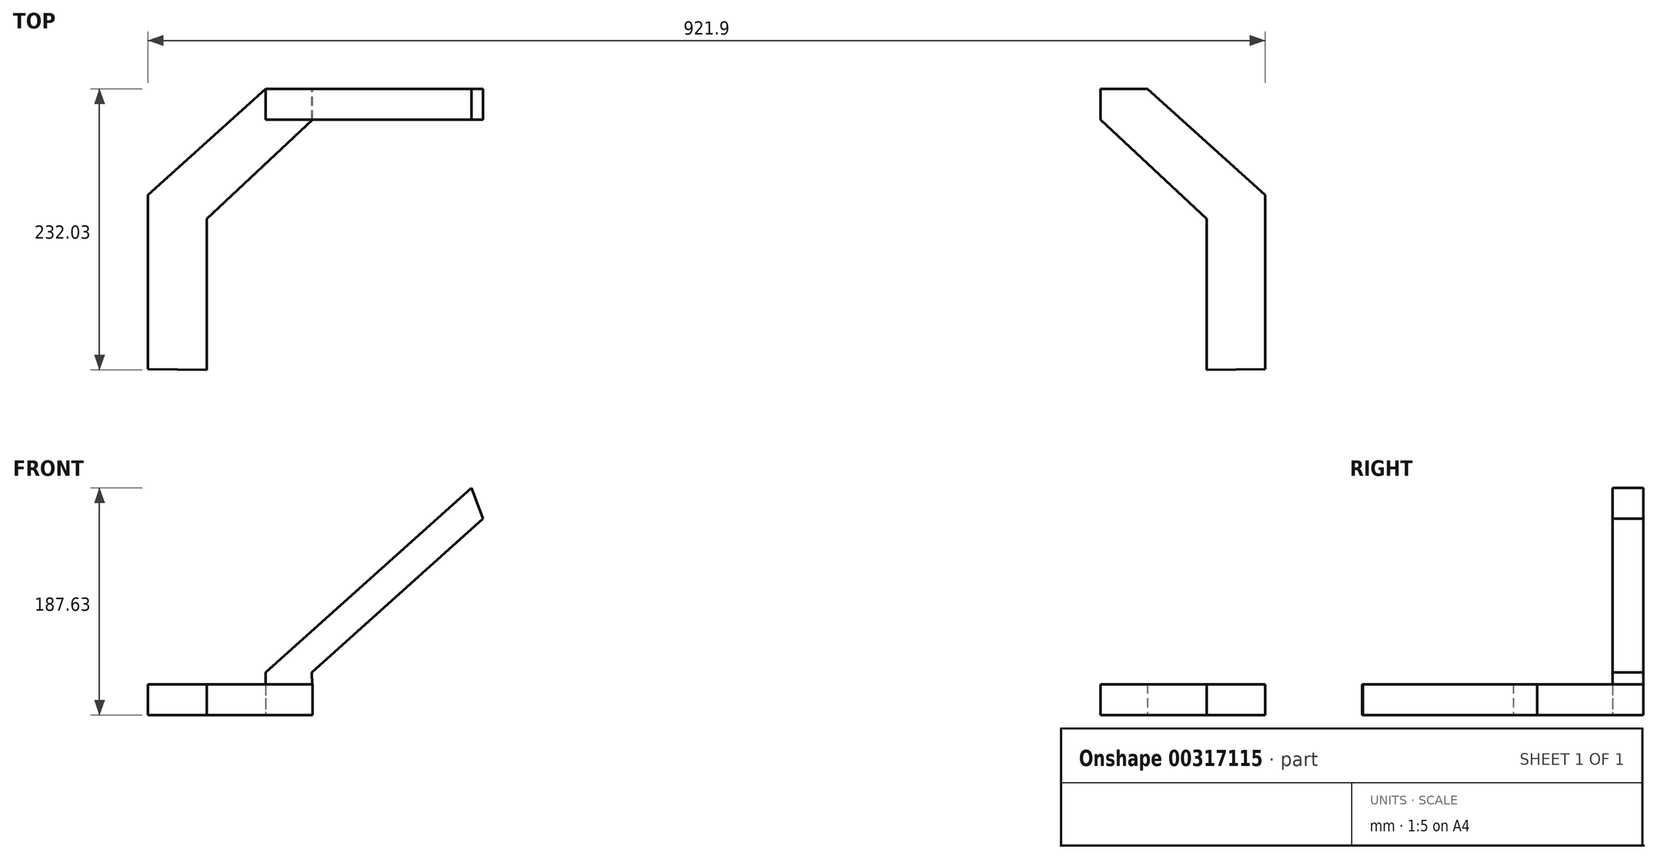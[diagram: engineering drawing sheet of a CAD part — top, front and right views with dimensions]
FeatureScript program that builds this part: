
annotation { "Feature Type Name" : "Feature", "Feature Type Description" : "" }
export const myFeature = defineFeature(function(context is Context, id is Id, definition is map)
    precondition{}
    {
        {
            var Q0;
            Q0=qCreatedBy(makeId("Front.planeOp"),FACE);
            var sketch = newSketch(context, id + "F0", { "sketchPlane" : qUnion([Q0])});
            skLineSegment(sketch, "E0.bottom", {"start": v(0, 127) * mm, "end": v(-184.37, 127) * mm});
            skLineSegment(sketch, "E0.top", {"start": v(0, 152.4) * mm, "end": v(-194.1, 152.4) * mm});
            skLineSegment(sketch, "E0.right", {"start": v(-184.37, 127) * mm, "end": v(-194.1, 152.4) * mm});
            skPoint(sketch, "E0.middle", {"position": v(0, 112.8) * mm});
            skLineSegment(sketch, "E1", {"start": v(-194.1, 152.4) * mm, "end": v(-363.8, 0) * mm});
            skLineSegment(sketch, "E2", {"start": v(-325.78, 0) * mm, "end": v(-184.37, 127) * mm});
            skLineSegment(sketch, "E3", {"start": v(0, 152.4) * mm, "end": v(0, 127) * mm});
            skLineSegment(sketch, "E4", {"start": v(-363.8, 0) * mm, "end": v(-363.8, -35.23) * mm});
            skLineSegment(sketch, "E5", {"start": v(-363.8, -35.23) * mm, "end": v(-325, -35.23) * mm});
            skLineSegment(sketch, "E6", {"start": v(-325, -35.23) * mm, "end": v(-325.78, 0) * mm});
            skLineSegment(sketch, "E7.MirrorCS", {"start": v(0, 152.4) * mm, "end": v(194.1, 152.4) * mm});
            skLineSegment(sketch, "E8.MirrorCS", {"start": v(194.1, 152.4) * mm, "end": v(363.8, 0) * mm});
            skLineSegment(sketch, "E9.MirrorCS", {"start": v(363.8, 0) * mm, "end": v(363.8, -35.23) * mm});
            skLineSegment(sketch, "E10.MirrorCS", {"start": v(363.8, -35.23) * mm, "end": v(325, -35.23) * mm});
            skLineSegment(sketch, "E11.MirrorCS", {"start": v(325, -35.23) * mm, "end": v(325.78, 0) * mm});
            skLineSegment(sketch, "E12.MirrorCS", {"start": v(325.78, 0) * mm, "end": v(184.37, 127) * mm});
            skLineSegment(sketch, "E13.MirrorCS", {"start": v(0, 127) * mm, "end": v(184.37, 127) * mm});
            skSolve(sketch);
        }
        {
            var Q0;
            Q0 = qSketchRegion(id + "F0", true);
            var sketch = newSketch(context, id + "F1", { "sketchPlane" : qUnion([Q0])});
            skSolve(sketch);
        }
        {
            var Q0;
            Q0=makeQuery(id+"F1.imprint","IMPRINT",FACE,{"disambiguationData":[TD([[makeQuery(id+"F1.imprint","IMPRINT",EDGE,{"derivedFrom":makeQuery(id+"F0.imprint","IMPRINT",EDGE,{"derivedFrom":sQuery(id+"F0.wireOp",EDGE,"E0.bottom")})}),-1.0]])]});
            var Q1;
            Q1=makeQuery(id+"F1.imprint","IMPRINT",FACE,{"disambiguationData":[TD([[makeQuery(id+"F1.imprint","IMPRINT",EDGE,{"derivedFrom":makeQuery(id+"F0.imprint","IMPRINT",EDGE,{"derivedFrom":sQuery(id+"F0.wireOp",EDGE,"E0.right")})}),1.0]])]});
            var Q2;
            Q2=makeQuery(id+"F1.imprint","IMPRINT",FACE,{"disambiguationData":[TD([[makeQuery(id+"F1.imprint","IMPRINT",EDGE,{"derivedFrom":makeQuery(id+"F0.imprint","IMPRINT",EDGE,{"derivedFrom":sQuery(id+"F0.wireOp",EDGE,"E3")})}),1.0]])]});
            extrude(context, id + "F2", {"entities" : qUnion([Q0, Q1, Q2]), "depth" : 25.4 * mm});
        }
        {
            var Q0;
            Q0=makeQuery(id+"F2.opExtrude","SWEPT_FACE",FACE,{"disambiguationData":[OSD([sQuery(id+"F0.wireOp",EDGE,"E5")])]});
            var sketch = newSketch(context, id + "F3", { "sketchPlane" : qUnion([Q0])});
            skLineSegment(sketch, "E14", {"start": v(-460.95, 87.67) * mm, "end": v(-363.8, 0) * mm});
            skLineSegment(sketch, "E15", {"start": v(-325, 25.4) * mm, "end": v(-412.58, 107.15) * mm});
            skLineSegment(sketch, "E16", {"start": v(-460.95, 87.67) * mm, "end": v(-460.95, 231.47) * mm});
            skLineSegment(sketch, "E17", {"start": v(-412.58, 107.15) * mm, "end": v(-412.58, 232.03) * mm});
            skLineSegment(sketch, "E18", {"start": v(-460.95, 231.47) * mm, "end": v(-412.58, 232.03) * mm});
            skLineSegment(sketch, "E19.MirrorCS", {"start": v(325, 25.4) * mm, "end": v(412.58, 107.15) * mm});
            skLineSegment(sketch, "E20.MirrorCS", {"start": v(460.95, 87.67) * mm, "end": v(363.8, 0) * mm});
            skLineSegment(sketch, "E21.MirrorCS", {"start": v(460.95, 87.67) * mm, "end": v(460.95, 231.47) * mm});
            skLineSegment(sketch, "E22.MirrorCS", {"start": v(460.95, 231.47) * mm, "end": v(412.58, 232.03) * mm});
            skLineSegment(sketch, "E23.MirrorCS", {"start": v(412.58, 107.15) * mm, "end": v(412.58, 232.03) * mm});
            skLineSegment(sketch, "E24", {"start": v(-325, 25.4) * mm, "end": v(-325, 0) * mm});
            skLineSegment(sketch, "E25", {"start": v(-325, 0) * mm, "end": v(-363.8, 0) * mm});
            skLineSegment(sketch, "E26.MirrorCS", {"start": v(325, 0) * mm, "end": v(363.8, 0) * mm});
            skLineSegment(sketch, "E27.MirrorCS", {"start": v(325, 25.4) * mm, "end": v(325, 0) * mm});
            skSolve(sketch);
        }
        {
            var Q0;
            Q0=makeQuery(id+"F3.imprint","IMPRINT",FACE,{"disambiguationData":[TD([[makeQuery(id+"F3.imprint","IMPRINT",EDGE,{"derivedFrom":sQuery(id+"F3.wireOp",EDGE,"E14")}),1.0]])]});
            var Q1;
            Q1=makeQuery(id+"F3.imprint","IMPRINT",FACE,{"disambiguationData":[TD([[makeQuery(id+"F3.imprint","IMPRINT",EDGE,{"derivedFrom":sQuery(id+"F3.wireOp",EDGE,"E20.MirrorCS")}),-1.0]])]});
            extrude(context, id + "F4", {"entities" : qUnion([Q0, Q1]), "oppositeDirection" : true, "depth" : 25.4 * mm});
        }
    });
